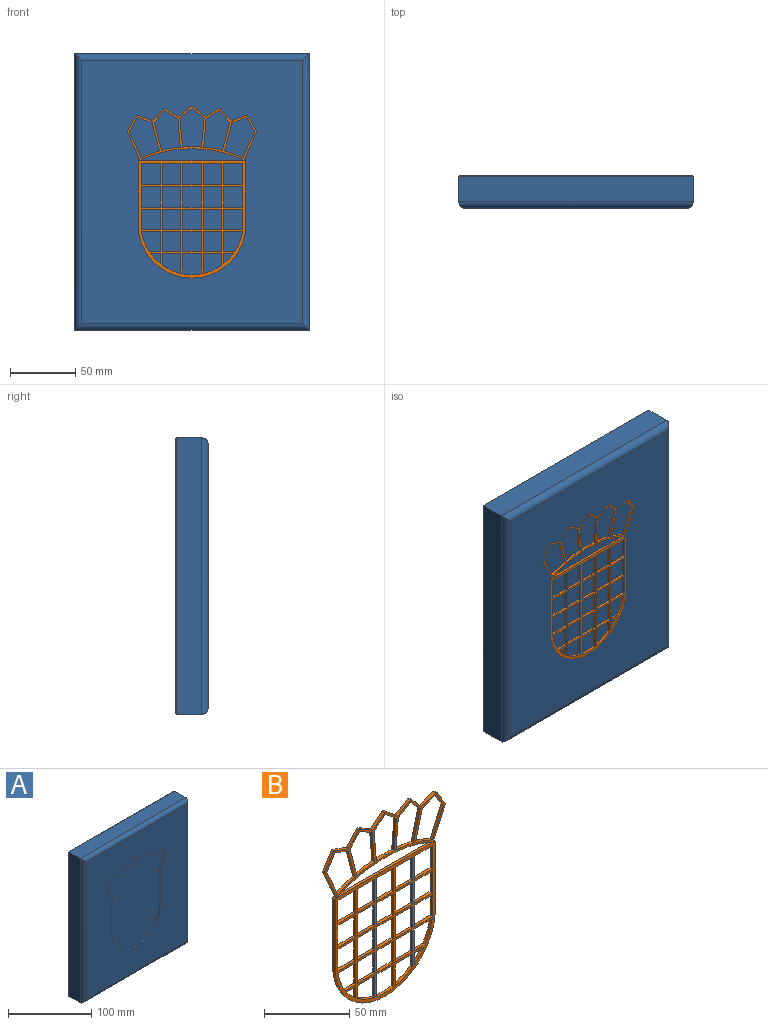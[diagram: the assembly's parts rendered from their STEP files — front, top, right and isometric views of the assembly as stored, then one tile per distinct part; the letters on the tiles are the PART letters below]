
ASSEMBLY  parts=2 mates=1
PART A: 58 faces, bbox 180x25x212.4 mm
  f0: plane 211.4x179mm, normal (0,1,0), area 36974mm2, adj f29,f31,f32,f33,f34,f35,f36,f37
  f1: plane 10.9x6.69mm, normal (0.85,0,-0.52), area 25.6mm2, adj f23,f24,f53,f54
  f2: plane 50.25x2mm, normal (1,0,0), area 100.5mm2, adj f6,f23,f24,f52
  f3: plane 50.25x2mm, normal (-1,0,0), area 100.5mm2, adj f5,f23,f24,f51
  f4: plane 10.9x6.69mm, normal (-0.85,0,-0.52), area 25.6mm2, adj f23,f24,f49,f50
  f5: cylinder r=41.6mm len=41.46mm, axis (0,1,0), area 125.6mm2, adj f3,f6,f23,f24
  f6: cylinder r=41.6mm len=41.46mm, axis (0,1,0), area 125.6mm2, adj f2,f5,f23,f24
  f7: plane 9.06x8.06mm, normal (-0.75,0,-0.66), area 24.2mm2, adj f8,f23,f24,f57
  f8: plane 11.32x4.12mm, normal (0.34,0,-0.94), area 24.1mm2, adj f7,f23,f24,f49
  f9: plane 21.77x9.85mm, normal (-0.91,0,0.41), area 47.8mm2, adj f10,f23,f24,f50
  f10: plane 2x0.33mm, normal (0,0,-1), area 0.7mm2, adj f9,f23,f24,f51
  f11: plane 2x0.33mm, normal (0,0,-1), area 0.7mm2, adj f12,f23,f24,f52
  f12: plane 21.77x9.85mm, normal (0.91,0,0.41), area 47.8mm2, adj f11,f23,f24,f53
  f13: plane 11.32x4.12mm, normal (-0.34,0,-0.94), area 24.1mm2, adj f14,f23,f24,f54
  f14: plane 9.06x8.06mm, normal (0.75,0,-0.66), area 24.2mm2, adj f13,f23,f24,f55
  f15: plane 10.42x6.08mm, normal (-0.5,0,-0.86), area 24.1mm2, adj f16,f23,f24,f55
  f16: plane 9.32x7.64mm, normal (0.63,0,-0.77), area 24.1mm2, adj f15,f23,f24,f56
  f17: plane 9.32x7.64mm, normal (-0.63,0,-0.77), area 24.1mm2, adj f22,f23,f24,f56
  f18: plane 180x19.5mm, normal (0,0,1), area 3510mm2, adj f19,f21,f26,f46
  f19: plane 212.4x19.5mm, normal (-1,0,0), area 4141.8mm2, adj f18,f20,f25,f48
  f20: plane 180x19.5mm, normal (0,0,-1), area 3510mm2, adj f19,f21,f27,f47
  f21: plane 212.4x19.5mm, normal (1,0,0), area 4141.8mm2, adj f18,f20,f28,f45
  f22: plane 10.42x6.08mm, normal (0.5,0,-0.86), area 24.1mm2, adj f17,f23,f24,f57
  f23: plane 202.4x170mm, normal (0,-1,0), area 24421.6mm2, adj f1,f2,f3,f4,f5,f6,f7,f8
  f24: plane 132.03x99.68mm, normal (0,-1,0), area 9986mm2, adj f1,f2,f3,f4,f5,f6,f7,f8
  f25: cylinder r=5mm len=212.4mm, axis (0,0,1), area 1639.6mm2, adj f19,f23,f26,f27
  f26: cylinder r=5mm len=180mm, axis (1,0,0), area 1385.2mm2, adj f18,f23,f25,f28
  f27: cylinder r=5mm len=180mm, axis (-1,0,0), area 1385.2mm2, adj f20,f23,f25,f28
  f28: cylinder r=5mm len=212.4mm, axis (0,0,-1), area 1639.6mm2, adj f21,f23,f26,f27
  f29: cylinder r=12.5mm len=25mm, axis (0,1,0), area 723.1mm2, adj f0,f30,f31,f39,f40
  f30: plane 25x25mm, normal (0,1,0), area 490.9mm2, adj f29
  f31: plane 10.41x2mm, normal (0,0,1), area 20.8mm2, adj f0,f29,f32,f40
  f32: cylinder r=3mm len=3mm, axis (0,1,0), area 9.4mm2, adj f0,f31,f33,f40
  f33: plane 4.5x2mm, normal (1,0,0), area 9mm2, adj f0,f32,f34,f40
  f34: cylinder r=3mm len=3mm, axis (0,1,0), area 9.4mm2, adj f0,f33,f35,f40
  f35: plane 44.5x2mm, normal (0,0,-1), area 89mm2, adj f0,f34,f36,f40
  f36: cylinder r=3mm len=3mm, axis (0,1,0), area 9.4mm2, adj f0,f35,f37,f40
  f37: plane 4.5x2mm, normal (-1,0,0), area 9mm2, adj f0,f36,f38,f40
  f38: cylinder r=3mm len=3mm, axis (0,1,0), area 9.4mm2, adj f0,f37,f39,f40
  f39: plane 10.41x2mm, normal (0,0,1), area 20.8mm2, adj f0,f29,f38,f40
  f40: plane 50.5x10.5mm, normal (0,1,0), area 361.2mm2, adj f29,f31,f32,f33,f34,f35,f36,f37
  f41: plane 3x3mm, normal (0,1,0), area 7.1mm2, adj f42
  f42: cylinder r=1.5mm len=8mm, axis (0,1,0), area 75.4mm2, adj f40,f41
  f43: plane 3x3mm, normal (0,1,0), area 7.1mm2, adj f44
  f44: cylinder r=1.5mm len=8mm, axis (0,1,0), area 75.4mm2, adj f40,f43
  f45: plane 212.4x0.5mm, normal (0.71,0.71,0), area 149.8mm2, adj f0,f21,f46,f47
  f46: plane 180x0.5mm, normal (0,0.71,0.71), area 126.9mm2, adj f0,f18,f45,f48
  f47: plane 180x0.5mm, normal (0,0.71,-0.71), area 126.9mm2, adj f0,f20,f45,f48
  f48: plane 212.4x0.5mm, normal (-0.71,0.71,0), area 149.8mm2, adj f0,f19,f46,f47
  f49: cylinder r=1.25mm len=2mm, axis (0,-1,0), area 3.4mm2, adj f4,f8,f23,f24
  f50: cylinder r=1.25mm len=2mm, axis (0,-1,0), area 2.4mm2, adj f4,f9,f23,f24
  f51: cylinder r=1.25mm len=2mm, axis (0,-1,0), area 3.9mm2, adj f3,f10,f23,f24
  f52: cylinder r=1.25mm len=2mm, axis (0,-1,0), area 3.9mm2, adj f2,f11,f23,f24
  f53: cylinder r=1.25mm len=2mm, axis (0,-1,0), area 2.4mm2, adj f1,f12,f23,f24
  f54: cylinder r=1.25mm len=2mm, axis (0,-1,0), area 3.4mm2, adj f1,f13,f23,f24
  f55: cylinder r=1.25mm len=2mm, axis (0,1,0), area 3.4mm2, adj f14,f15,f23,f24
  f56: cylinder r=1.25mm len=2mm, axis (0,1,0), area 3.4mm2, adj f16,f17,f23,f24
  f57: cylinder r=1.25mm len=2mm, axis (0,1,0), area 3.4mm2, adj f7,f22,f23,f24
PART B: 159 faces, bbox 99.7x2x132 mm
  f0: plane 16.55x2mm, normal (1,0,0), area 33.1mm2, adj f1,f147,f148,f149
  f1: plane 14.86x2mm, normal (0,0,-1), area 29.7mm2, adj f0,f2,f148,f149
  f2: plane 16.55x2mm, normal (-1,0,0), area 33.1mm2, adj f1,f147,f148,f149
  f3: plane 15.61x2mm, normal (1,0,0), area 31.2mm2, adj f4,f116,f148,f149
  f4: plane 14.29x2mm, normal (0,0,-1), area 28.6mm2, adj f3,f5,f148,f149
  f5: plane 15.61x2mm, normal (-1,0,0), area 31.2mm2, adj f4,f116,f148,f149
  f6: plane 15.55x2mm, normal (1,0,0), area 31.1mm2, adj f7,f117,f148,f149
  f7: plane 14.29x2mm, normal (0,0,-1), area 28.6mm2, adj f6,f8,f148,f149
  f8: plane 15.55x2mm, normal (-1,0,0), area 31.1mm2, adj f7,f117,f148,f149
  f9: plane 10.9x6.69mm, normal (-0.85,0,0.52), area 25.6mm2, adj f148,f149,f150,f158
  f10: plane 21.77x9.85mm, normal (-0.91,0,-0.41), area 47.8mm2, adj f11,f148,f149,f150
  f11: plane 2x0.33mm, normal (0,0,1), area 0.7mm2, adj f10,f148,f149,f151
  f12: plane 50.25x2mm, normal (-1,0,0), area 100.5mm2, adj f13,f148,f149,f151
  f13: cylinder r=41.6mm len=41.46mm, axis (0,1,0), area 125.6mm2, adj f12,f14,f148,f149
  f14: cylinder r=41.6mm len=41.46mm, axis (0,1,0), area 125.6mm2, adj f13,f15,f148,f149
  f15: plane 50.25x2mm, normal (1,0,0), area 100.5mm2, adj f14,f148,f149,f152
  f16: plane 2x0.33mm, normal (0,0,1), area 0.7mm2, adj f17,f148,f149,f152
  f17: plane 21.77x9.85mm, normal (0.91,0,-0.41), area 47.8mm2, adj f16,f148,f149,f153
  f18: plane 10.9x6.69mm, normal (0.85,0,0.52), area 25.6mm2, adj f148,f149,f153,f154
  f19: plane 11.32x4.12mm, normal (-0.34,0,0.94), area 24.1mm2, adj f20,f148,f149,f154
  f20: plane 9.06x8.06mm, normal (0.75,0,0.66), area 24.2mm2, adj f19,f148,f149,f155
  f21: plane 10.42x6.08mm, normal (-0.5,0,0.86), area 24.1mm2, adj f22,f148,f149,f155
  f22: plane 9.32x7.64mm, normal (0.63,0,0.77), area 24.1mm2, adj f21,f148,f149,f156
  f23: plane 9.32x7.64mm, normal (-0.63,0,0.77), area 24.1mm2, adj f24,f148,f149,f156
  f24: plane 10.42x6.08mm, normal (0.5,0,0.86), area 24.1mm2, adj f23,f148,f149,f157
  f25: plane 9.06x8.06mm, normal (-0.75,0,0.66), area 24.2mm2, adj f118,f148,f149,f157
  f26: cylinder r=89.8mm len=14.4mm, axis (0,1,0), area 29.2mm2, adj f27,f119,f148,f149
  f27: plane 22.21x2mm, normal (1,0,-0.08), area 44.6mm2, adj f26,f28,f148,f149
  f28: plane 10.24x5.98mm, normal (0.5,0,-0.86), area 23.7mm2, adj f27,f29,f148,f149
  f29: plane 8.88x7.9mm, normal (-0.75,0,-0.66), area 23.8mm2, adj f28,f119,f148,f149
  f30: plane 15.55x2mm, normal (1,0,0), area 31.1mm2, adj f31,f120,f148,f149
  f31: plane 13.92x2mm, normal (0,0,-1), area 27.8mm2, adj f30,f32,f148,f149
  f32: plane 15.55x2mm, normal (-1,0,0), area 31.1mm2, adj f31,f120,f148,f149
  f33: plane 13.92x2mm, normal (0,0,-1), area 27.8mm2, adj f34,f121,f148,f149
  f34: plane 15.61x2mm, normal (-1,0,0), area 31.2mm2, adj f33,f35,f148,f149
  f35: plane 13.92x2mm, normal (0,0,1), area 27.8mm2, adj f34,f121,f148,f149
  f36: plane 16.55x2mm, normal (1,0,0), area 33.1mm2, adj f37,f122,f148,f149
  f37: plane 14.86x2mm, normal (0,0,-1), area 29.7mm2, adj f36,f38,f148,f149
  f38: plane 16.55x2mm, normal (-1,0,0), area 33.1mm2, adj f37,f122,f148,f149
  f39: plane 21.71x5.63mm, normal (0.97,0,-0.25), area 44.8mm2, adj f40,f123,f148,f149
  f40: plane 11.11x4.04mm, normal (0.34,0,-0.94), area 23.6mm2, adj f39,f41,f148,f149
  f41: plane 10.61x6.51mm, normal (-0.85,0,-0.52), area 24.9mm2, adj f40,f42,f148,f149
  f42: plane 20.26x9.17mm, normal (-0.91,0,0.41), area 44.5mm2, adj f41,f123,f148,f149
  f43: cylinder r=0.36mm len=2mm, axis (0,1,0), area 1.6mm2, adj f44,f124,f148,f149
  f44: cylinder r=88.3mm len=38.52mm, axis (0,1,0), area 79.4mm2, adj f43,f45,f148,f149
  f45: cylinder r=88.3mm len=38.52mm, axis (0,1,0), area 79.4mm2, adj f44,f46,f148,f149
  f46: cylinder r=0.36mm len=2mm, axis (0,1,0), area 1.6mm2, adj f45,f124,f148,f149
  f47: plane 16.55x2mm, normal (1,0,0), area 33.1mm2, adj f48,f125,f148,f149
  f48: plane 13.92x2mm, normal (0,0,-1), area 27.8mm2, adj f47,f49,f148,f149
  f49: plane 16.55x2mm, normal (-1,0,0), area 33.1mm2, adj f48,f125,f148,f149
  f50: plane 14.29x2mm, normal (0,0,1), area 28.6mm2, adj f51,f126,f148,f149
  f51: plane 16.55x2mm, normal (1,0,0), area 33.1mm2, adj f50,f52,f148,f149
  f52: plane 14.29x2mm, normal (0,0,-1), area 28.6mm2, adj f51,f126,f148,f149
  f53: plane 15.61x2mm, normal (1,0,0), area 31.2mm2, adj f54,f127,f148,f149
  f54: plane 14.86x2mm, normal (0,0,-1), area 29.7mm2, adj f53,f55,f148,f149
  f55: plane 15.61x2mm, normal (-1,0,0), area 31.2mm2, adj f54,f127,f148,f149
  f56: plane 15.55x2mm, normal (1,0,0), area 31.1mm2, adj f57,f128,f148,f149
  f57: plane 14.86x2mm, normal (0,0,-1), area 29.7mm2, adj f56,f58,f148,f149
  f58: plane 15.55x2mm, normal (-1,0,0), area 31.1mm2, adj f57,f128,f148,f149
  f59: cylinder r=39.76mm len=15.59mm, axis (0,1,0), area 33.6mm2, adj f60,f129,f148,f149
  f60: plane 14.75x2mm, normal (0,0,-1), area 29.5mm2, adj f59,f61,f148,f149
  f61: plane 15.59x2mm, normal (-1,0,0), area 31.2mm2, adj f60,f129,f148,f149
  f62: plane 8.1x2mm, normal (1,0,0), area 16.2mm2, adj f63,f130,f148,f149
  f63: plane 7.76x2mm, normal (0,0,-1), area 15.5mm2, adj f62,f130,f148,f149
  f64: plane 15.6x2mm, normal (1,0,0), area 31.2mm2, adj f65,f131,f148,f149
  f65: plane 14.29x2mm, normal (0,0,-1), area 28.6mm2, adj f64,f66,f148,f149
  f66: plane 9.22x2mm, normal (-1,0,0), area 18.4mm2, adj f65,f131,f148,f149
  f67: plane 15.91x2mm, normal (1,0,0), area 31.8mm2, adj f68,f132,f148,f149
  f68: plane 13.92x2mm, normal (0,0,-1), area 27.8mm2, adj f67,f69,f148,f149
  f69: plane 15.91x2mm, normal (-1,0,0), area 31.8mm2, adj f68,f70,f148,f149
  f70: cylinder r=39.76mm len=6.96mm, axis (0,1,0), area 14mm2, adj f69,f132,f148,f149
  f71: plane 14.86x2mm, normal (0,0,-1), area 29.7mm2, adj f72,f133,f148,f149
  f72: plane 15.61x2mm, normal (-1,0,0), area 31.2mm2, adj f71,f73,f148,f149
  f73: plane 14.86x2mm, normal (0,0,1), area 29.7mm2, adj f72,f133,f148,f149
  f74: plane 14.86x2mm, normal (0,0,-1), area 29.7mm2, adj f75,f134,f148,f149
  f75: plane 15.55x2mm, normal (-1,0,0), area 31.1mm2, adj f74,f76,f148,f149
  f76: plane 14.86x2mm, normal (0,0,1), area 29.7mm2, adj f75,f134,f148,f149
  f77: cylinder r=39.76mm len=8.1mm, axis (0,1,0), area 22.5mm2, adj f78,f135,f148,f149
  f78: plane 7.76x2mm, normal (0,0,-1), area 15.5mm2, adj f77,f135,f148,f149
  f79: plane 9.22x2mm, normal (1,0,0), area 18.4mm2, adj f80,f136,f148,f149
  f80: plane 14.29x2mm, normal (0,0,-1), area 28.6mm2, adj f79,f81,f148,f149
  f81: plane 15.6x2mm, normal (-1,0,0), area 31.2mm2, adj f80,f136,f148,f149
  f82: plane 15.59x2mm, normal (1,0,0), area 31.2mm2, adj f83,f137,f148,f149
  f83: plane 14.29x2mm, normal (0,0,-1), area 28.6mm2, adj f82,f84,f148,f149
  f84: plane 15.59x2mm, normal (-1,0,0), area 31.2mm2, adj f83,f137,f148,f149
  f85: plane 15.59x2mm, normal (-1,0,0), area 31.2mm2, adj f86,f138,f148,f149
  f86: plane 14.29x2mm, normal (0,0,1), area 28.6mm2, adj f85,f87,f148,f149
  f87: plane 15.59x2mm, normal (1,0,0), area 31.2mm2, adj f86,f138,f148,f149
  f88: plane 14.75x2mm, normal (0,0,-1), area 29.5mm2, adj f89,f139,f148,f149
  f89: cylinder r=39.76mm len=15.59mm, axis (0,1,0), area 33.6mm2, adj f88,f90,f148,f149
  f90: plane 8.79x2mm, normal (0,0,1), area 17.6mm2, adj f89,f139,f148,f149
  f91: plane 16.55x2mm, normal (-1,0,0), area 33.1mm2, adj f92,f140,f148,f149
  f92: plane 14.29x2mm, normal (0,0,1), area 28.6mm2, adj f91,f93,f148,f149
  f93: plane 16.55x2mm, normal (1,0,0), area 33.1mm2, adj f92,f140,f148,f149
  f94: plane 14.29x2mm, normal (0,0,-1), area 28.6mm2, adj f95,f141,f148,f149
  f95: plane 15.55x2mm, normal (-1,0,0), area 31.1mm2, adj f94,f96,f148,f149
  f96: plane 14.29x2mm, normal (0,0,1), area 28.6mm2, adj f95,f141,f148,f149
  f97: plane 15.61x2mm, normal (-1,0,0), area 31.2mm2, adj f98,f142,f148,f149
  f98: plane 14.29x2mm, normal (0,0,1), area 28.6mm2, adj f97,f99,f148,f149
  f99: plane 15.61x2mm, normal (1,0,0), area 31.2mm2, adj f98,f142,f148,f149
  f100: plane 15.59x2mm, normal (1,0,0), area 31.2mm2, adj f101,f143,f148,f149
  f101: plane 13.92x2mm, normal (0,0,-1), area 27.8mm2, adj f100,f102,f148,f149
  f102: plane 15.59x2mm, normal (-1,0,0), area 31.2mm2, adj f101,f143,f148,f149
  f103: plane 8.88x7.9mm, normal (0.75,0,-0.66), area 23.8mm2, adj f104,f144,f148,f149
  f104: plane 10.24x5.98mm, normal (-0.5,0,-0.86), area 23.7mm2, adj f103,f105,f148,f149
  f105: plane 22.21x2mm, normal (-1,0,-0.08), area 44.6mm2, adj f104,f106,f148,f149
  f106: cylinder r=89.8mm len=14.4mm, axis (0,1,0), area 29.2mm2, adj f105,f144,f148,f149
  f107: plane 20.26x9.17mm, normal (0.91,0,0.41), area 44.5mm2, adj f108,f145,f148,f149
  f108: plane 10.61x6.51mm, normal (0.85,0,-0.52), area 24.9mm2, adj f107,f109,f148,f149
  f109: plane 11.11x4.04mm, normal (-0.34,0,-0.94), area 23.6mm2, adj f108,f110,f148,f149
  f110: plane 21.71x5.63mm, normal (-0.97,0,-0.25), area 44.8mm2, adj f109,f145,f148,f149
  f111: cylinder r=89.8mm len=7.34mm, axis (0,1,0), area 14.7mm2, adj f112,f146,f148,f149
  f112: cylinder r=89.8mm len=7.34mm, axis (0,1,0), area 14.7mm2, adj f111,f113,f148,f149
  f113: plane 22.17x2mm, normal (1,0,0.08), area 44.5mm2, adj f112,f114,f148,f149
  f114: plane 9.23x7.57mm, normal (0.63,0,-0.77), area 23.9mm2, adj f113,f115,f148,f149
  f115: plane 9.23x7.57mm, normal (-0.63,0,-0.77), area 23.9mm2, adj f114,f146,f148,f149
  f116: plane 14.29x2mm, normal (0,0,1), area 28.6mm2, adj f3,f5,f148,f149
  f117: plane 14.29x2mm, normal (0,0,1), area 28.6mm2, adj f6,f8,f148,f149
  f118: plane 11.32x4.12mm, normal (0.34,0,0.94), area 24.1mm2, adj f25,f148,f149,f158
  f119: plane 21.7x5.63mm, normal (-0.97,0,0.25), area 44.8mm2, adj f26,f29,f148,f149
  f120: plane 13.92x2mm, normal (0,0,1), area 27.8mm2, adj f30,f32,f148,f149
  f121: plane 15.61x2mm, normal (1,0,0), area 31.2mm2, adj f33,f35,f148,f149
  f122: plane 14.86x2mm, normal (0,0,1), area 29.7mm2, adj f36,f38,f148,f149
  f123: cylinder r=89.8mm len=14.08mm, axis (0,1,0), area 30mm2, adj f39,f42,f148,f149
  f124: plane 77.05x2mm, normal (0,0,1), area 154.1mm2, adj f43,f46,f148,f149
  f125: plane 13.92x2mm, normal (0,0,1), area 27.8mm2, adj f47,f49,f148,f149
  f126: plane 16.55x2mm, normal (-1,0,0), area 33.1mm2, adj f50,f52,f148,f149
  f127: plane 14.86x2mm, normal (0,0,1), area 29.7mm2, adj f53,f55,f148,f149
  f128: plane 14.86x2mm, normal (0,0,1), area 29.7mm2, adj f56,f58,f148,f149
  f129: plane 8.79x2mm, normal (0,0,1), area 17.6mm2, adj f59,f61,f148,f149
  f130: cylinder r=39.76mm len=8.1mm, axis (0,1,0), area 22.5mm2, adj f62,f63,f148,f149
  f131: cylinder r=39.76mm len=14.29mm, axis (0,1,0), area 31.5mm2, adj f64,f66,f148,f149
  f132: cylinder r=39.76mm len=6.96mm, axis (0,1,0), area 14mm2, adj f67,f70,f148,f149
  f133: plane 15.61x2mm, normal (1,0,0), area 31.2mm2, adj f71,f73,f148,f149
  f134: plane 15.55x2mm, normal (1,0,0), area 31.1mm2, adj f74,f76,f148,f149
  f135: plane 8.1x2mm, normal (-1,0,0), area 16.2mm2, adj f77,f78,f148,f149
  f136: cylinder r=39.76mm len=14.29mm, axis (0,1,0), area 31.5mm2, adj f79,f81,f148,f149
  f137: plane 14.29x2mm, normal (0,0,1), area 28.6mm2, adj f82,f84,f148,f149
  f138: plane 14.29x2mm, normal (0,0,-1), area 28.6mm2, adj f85,f87,f148,f149
  f139: plane 15.59x2mm, normal (1,0,0), area 31.2mm2, adj f88,f90,f148,f149
  f140: plane 14.29x2mm, normal (0,0,-1), area 28.6mm2, adj f91,f93,f148,f149
  f141: plane 15.55x2mm, normal (1,0,0), area 31.1mm2, adj f94,f96,f148,f149
  f142: plane 14.29x2mm, normal (0,0,-1), area 28.6mm2, adj f97,f99,f148,f149
  f143: plane 13.92x2mm, normal (0,0,1), area 27.8mm2, adj f100,f102,f148,f149
  f144: plane 21.7x5.63mm, normal (0.97,0,0.25), area 44.8mm2, adj f103,f106,f148,f149
  f145: cylinder r=89.8mm len=14.08mm, axis (0,1,0), area 30mm2, adj f107,f110,f148,f149
  f146: plane 22.17x2mm, normal (-1,0,0.08), area 44.5mm2, adj f111,f115,f148,f149
  f147: plane 14.86x2mm, normal (0,0,1), area 29.7mm2, adj f0,f2,f148,f149
  f148: plane 132.03x99.68mm, normal (0,-1,0), area 2153.9mm2, adj f0,f1,f2,f3,f4,f5,f6,f7
  f149: plane 132.03x99.68mm, normal (0,1,0), area 2153.9mm2, adj f0,f1,f2,f3,f4,f5,f6,f7
  f150: cylinder r=1.25mm len=2mm, axis (0,1,0), area 2.4mm2, adj f9,f10,f148,f149
  f151: cylinder r=1.25mm len=2mm, axis (0,1,0), area 3.9mm2, adj f11,f12,f148,f149
  f152: cylinder r=1.25mm len=2mm, axis (0,1,0), area 3.9mm2, adj f15,f16,f148,f149
  f153: cylinder r=1.25mm len=2mm, axis (0,1,0), area 2.4mm2, adj f17,f18,f148,f149
  f154: cylinder r=1.25mm len=2mm, axis (0,1,0), area 3.4mm2, adj f18,f19,f148,f149
  f155: cylinder r=1.25mm len=2mm, axis (0,-1,0), area 3.4mm2, adj f20,f21,f148,f149
  f156: cylinder r=1.25mm len=2mm, axis (0,-1,0), area 3.4mm2, adj f22,f23,f148,f149
  f157: cylinder r=1.25mm len=2mm, axis (0,-1,0), area 3.4mm2, adj f24,f25,f148,f149
  f158: cylinder r=1.25mm len=2mm, axis (0,1,0), area 3.4mm2, adj f9,f118,f148,f149
PLACE A t=(209.04,137.08,109.68)mm
PLACE B t=(209.04,114.08,109.68)mm
MATE fastened A.f23 <-> B.f148  axis (0,-1,0) through (209.04,112.08,43.39)mm
